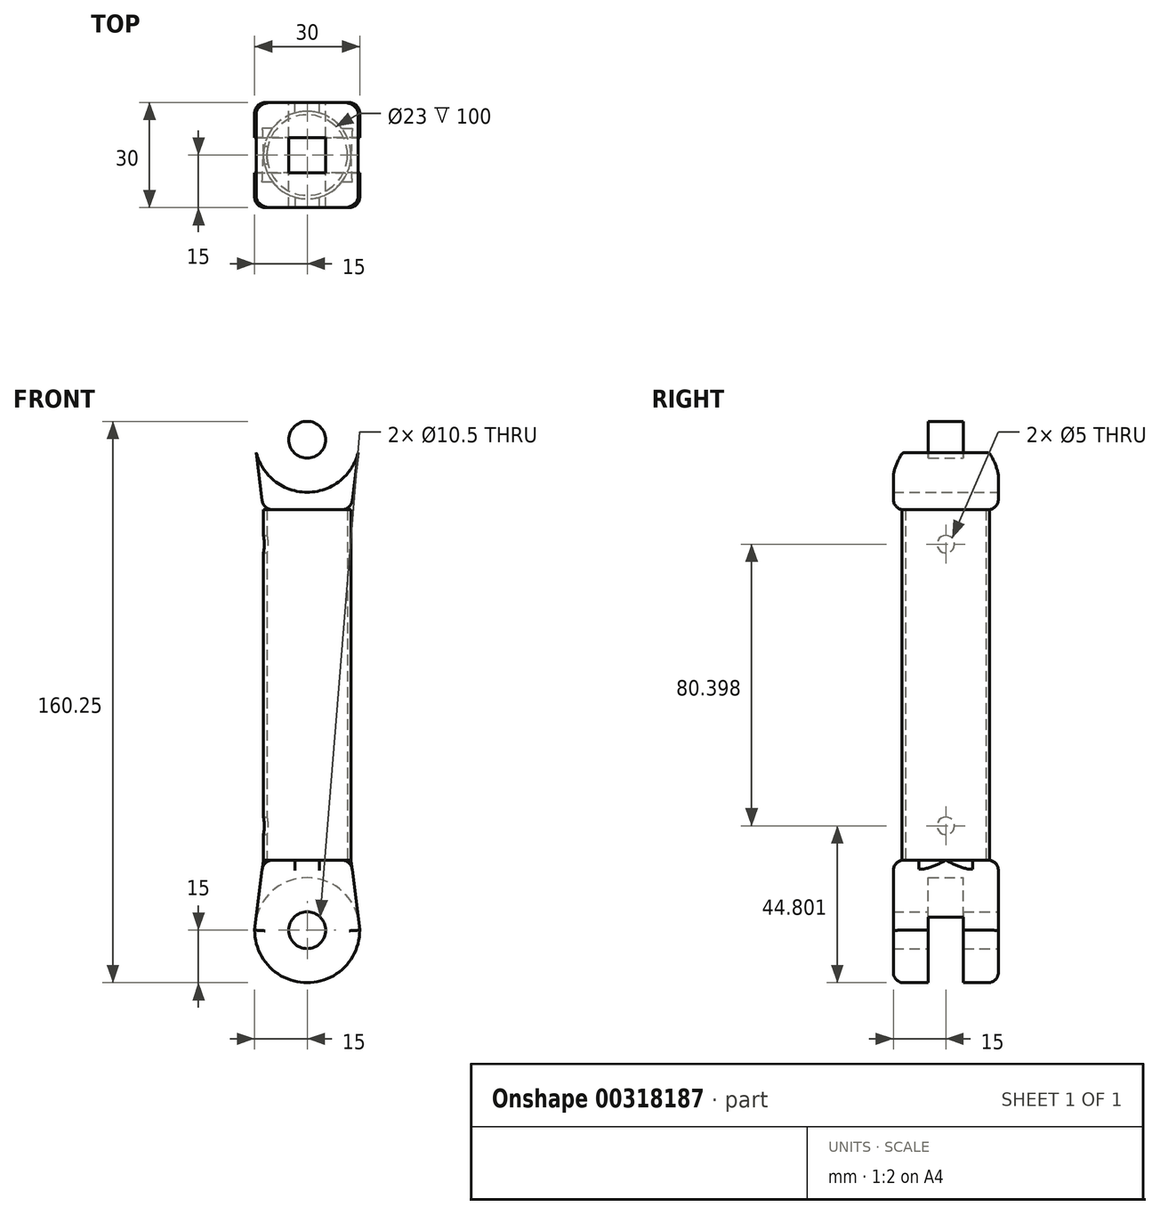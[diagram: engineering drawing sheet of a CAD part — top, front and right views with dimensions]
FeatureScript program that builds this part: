
annotation { "Feature Type Name" : "Feature", "Feature Type Description" : "" }
export const myFeature = defineFeature(function(context is Context, id is Id, definition is map)
    precondition{}
    {
        {
            var Q0;
            Q0=qCreatedBy(makeId("Front.planeOp"),FACE);
            var sketch = newSketch(context, id + "F0", { "sketchPlane" : qUnion([Q0])});
            skCircle(sketch, "E0", {"center": v(0, -70) * mm, "radius": 5.25 * mm});
            skCircle(sketch, "E1", {"center": v(0, -70) * mm, "radius": 15 * mm});
            skLineSegment(sketch, "E2", {"start": v(-12.5, -50) * mm, "end": v(12.5, -50) * mm});
            skLineSegment(sketch, "E3", {"start": v(-15, -69.99) * mm, "end": v(-12.5, -50) * mm});
            skLineSegment(sketch, "E4", {"start": v(15, -69.99) * mm, "end": v(12.5, -50) * mm});
            skCircle(sketch, "E5.MirrorC", {"center": v(0, 70) * mm, "radius": 15 * mm});
            skLineSegment(sketch, "E6.MirrorCS", {"start": v(15, 69.99) * mm, "end": v(12.5, 50) * mm});
            skLineSegment(sketch, "E7.MirrorCS", {"start": v(-12.5, 50) * mm, "end": v(12.5, 50) * mm});
            skLineSegment(sketch, "E8.MirrorCS", {"start": v(-15, 69.99) * mm, "end": v(-12.5, 50) * mm});
            skCircle(sketch, "E9.MirrorC", {"center": v(0, 70) * mm, "radius": 5.25 * mm});
            skSolve(sketch);
        }
        {
            var Q0;
            {var subQ5=sQuery(id+"F0.wireOp",EDGE,"E2");Q0=makeQuery(id+"F0.imprint","IMPRINT",FACE,{"disambiguationData":[TD([[makeQuery(id+"F0.imprint","IMPRINT",EDGE,{"derivedFrom":subQ5}),-1.0]])]});}
            var Q1;
            Q1=makeQuery(id+"F0.imprint","IMPRINT",FACE,{"disambiguationData":[TD([[makeQuery(id+"F0.imprint","IMPRINT",EDGE,{"derivedFrom":sQuery(id+"F0.wireOp",EDGE,"E0")}),-1.0]])]});
            extrude(context, id + "F1", {"entities" : qUnion([Q0, Q1]), "endBound" : BoundingType.SYMMETRIC, "depth" : 30 * mm});
        }
        {
            var Q0;
            Q0=qCreatedBy(makeId("Right.planeOp"),FACE);
            var sketch = newSketch(context, id + "F2", { "sketchPlane" : qUnion([Q0])});
            skLineSegment(sketch, "E10", {"start": v(0, -85) * mm, "end": v(5, -85) * mm});
            skLineSegment(sketch, "E11", {"start": v(5, -85) * mm, "end": v(5, -55) * mm});
            skLineSegment(sketch, "E12", {"start": v(5, -55) * mm, "end": v(-5, -55) * mm});
            skLineSegment(sketch, "E13", {"start": v(-5, -55) * mm, "end": v(-5, -85) * mm});
            skLineSegment(sketch, "E14", {"start": v(-5, -85) * mm, "end": v(0, -85) * mm});
            skSolve(sketch);
        }
        {
            var Q0;
            Q0 = qSketchRegion(id + "F2", true);
            extrude(context, id + "F3", {"entities" : qUnion([Q0]), "operationType" : NewBodyOperationType.REMOVE, "endBound" : BoundingType.SYMMETRIC, "oppositeDirection" : true, "depth" : 100 * mm});
        }
        {
            var Q0;
            {var subQ5=sQuery(id+"F0.wireOp",EDGE,"E2");Q0=makeQuery(id+"F0.imprint","IMPRINT",FACE,{"disambiguationData":[TD([[makeQuery(id+"F0.imprint","IMPRINT",EDGE,{"derivedFrom":subQ5}),-1.0]])]});}
            extrude(context, id + "F4", {"entities" : qUnion([Q0]), "operationType" : NewBodyOperationType.ADD, "endBound" : BoundingType.SYMMETRIC, "depth" : 25 * mm});
        }
        {
            var Q0;
            Q0=makeQuery(id+"F0.imprint","IMPRINT",FACE,{"disambiguationData":[TD([[makeQuery(id+"F0.imprint","IMPRINT",EDGE,{"derivedFrom":sQuery(id+"F0.wireOp",EDGE,"E9.MirrorC")}),1.0]])]});
            extrude(context, id + "F5", {"entities" : qUnion([Q0]), "endBound" : BoundingType.SYMMETRIC, "depth" : 10 * mm});
        }
        {
            var Q0;
            {var subQ5=sQuery(id+"F0.wireOp",EDGE,"E7.MirrorCS");Q0=makeQuery(id+"F0.imprint","IMPRINT",FACE,{"disambiguationData":[TD([[makeQuery(id+"F0.imprint","IMPRINT",EDGE,{"derivedFrom":subQ5}),1.0]])]});}
            extrude(context, id + "F6", {"entities" : qUnion([Q0]), "operationType" : NewBodyOperationType.ADD, "endBound" : BoundingType.SYMMETRIC, "depth" : 30 * mm});
        }
        {
            var Q0;
            Q0=qCreatedBy(makeId("Top.planeOp"),FACE);
            var sketch = newSketch(context, id + "F7", { "sketchPlane" : qUnion([Q0])});
            skCircle(sketch, "E15", {"center": v(0, 0) * mm, "radius": 12.5 * mm});
            skCircle(sketch, "E16", {"center": v(0, 0) * mm, "radius": 11.5 * mm});
            skSolve(sketch);
        }
        {
            var Q0;
            Q0 = qSketchRegion(id + "F7", true);
            extrude(context, id + "F8", {"entities" : qUnion([Q0]), "endBound" : BoundingType.SYMMETRIC, "depth" : 100 * mm});
        }
        {
            var Q0;
            Q0=makeQuery(id+"F1.opExtrude","SWEPT_BODY",BODY,{"disambiguationData":[OSD([sQuery(id+"F0.wireOp",EDGE,"E0"),sQuery(id+"F0.wireOp",EDGE,"E1"),sQuery(id+"F0.wireOp",EDGE,"E2"),sQuery(id+"F0.wireOp",EDGE,"E3"),sQuery(id+"F0.wireOp",EDGE,"E4")])]});
            var Q1;
            Q1=makeQuery(id+"F5.opExtrude","SWEPT_BODY",BODY,{"disambiguationData":[OSD([sQuery(id+"F0.wireOp",EDGE,"E5.MirrorC"),sQuery(id+"F0.wireOp",EDGE,"E6.MirrorCS"),sQuery(id+"F0.wireOp",EDGE,"E8.MirrorCS"),sQuery(id+"F0.wireOp",EDGE,"E9.MirrorC")])]});
            var Q2;
            Q2=makeQuery(id+"F8.opExtrude","SWEPT_BODY",BODY,{"disambiguationData":[OSD([sQuery(id+"F7.wireOp",EDGE,"E15"),sQuery(id+"F7.wireOp",EDGE,"E16")])]});
            booleanBodies(context, id + "F9", {"operationType" : BooleanOperationType.UNION, "tools" : qUnion([Q0, Q1, Q2])});
        }
        {
            var Q0;
            {var subQ0=sQuery(id+"F0.wireOp",EDGE,"E4");var subQ1=sQuery(id+"F0.wireOp",EDGE,"E2");Q0=makeQuery(id+"F9.opBoolean","SPLIT",EDGE,{"disambiguationData":[TD([makeQuery(id+"F1.opExtrude","CAP_FACE",FACE,{"disambiguationData":[OSD([sQuery(id+"F0.wireOp",EDGE,"E0"),sQuery(id+"F0.wireOp",EDGE,"E1"),subQ1,sQuery(id+"F0.wireOp",EDGE,"E3"),subQ0])],"isStart":true})])],"derivedFrom":makeQuery(id+"F1.opExtrude","SWEPT_EDGE",EDGE,{"disambiguationData":[OSD([subQ1,subQ0])]})});}
            var Q1;
            Q1=makeQuery(id+"F1.opExtrude","CAP_EDGE",EDGE,{"disambiguationData":[OSD([sQuery(id+"F0.wireOp",EDGE,"E4")])],"isStart":true});
            var Q2;
            Q2=makeQuery(id+"F1.opExtrude","CAP_EDGE",EDGE,{"disambiguationData":[OSD([sQuery(id+"F0.wireOp",EDGE,"E1")])],"isStart":true});
            var Q3;
            Q3=makeQuery(id+"F1.opExtrude","CAP_EDGE",EDGE,{"disambiguationData":[OSD([sQuery(id+"F0.wireOp",EDGE,"E3")])],"isStart":true});
            var Q4;
            Q4=makeQuery(id+"F1.opExtrude","CAP_EDGE",EDGE,{"disambiguationData":[OSD([sQuery(id+"F0.wireOp",EDGE,"E2")])],"isStart":true});
            var Q5;
            {var subQ0=sQuery(id+"F0.wireOp",EDGE,"E3");var subQ1=sQuery(id+"F0.wireOp",EDGE,"E2");Q5=makeQuery(id+"F9.opBoolean","SPLIT",EDGE,{"disambiguationData":[TD([makeQuery(id+"F1.opExtrude","CAP_FACE",FACE,{"disambiguationData":[OSD([sQuery(id+"F0.wireOp",EDGE,"E0"),sQuery(id+"F0.wireOp",EDGE,"E1"),subQ1,subQ0,sQuery(id+"F0.wireOp",EDGE,"E4")])],"isStart":true})])],"derivedFrom":makeQuery(id+"F1.opExtrude","SWEPT_EDGE",EDGE,{"disambiguationData":[OSD([subQ1,subQ0])]})});}
            var Q6;
            Q6=makeQuery(id+"F1.opExtrude","CAP_EDGE",EDGE,{"disambiguationData":[OSD([sQuery(id+"F0.wireOp",EDGE,"E3")])],"isStart":false});
            var Q7;
            Q7=makeQuery(id+"F1.opExtrude","CAP_EDGE",EDGE,{"disambiguationData":[OSD([sQuery(id+"F0.wireOp",EDGE,"E1")])],"isStart":false});
            var Q8;
            Q8=makeQuery(id+"F1.opExtrude","CAP_EDGE",EDGE,{"disambiguationData":[OSD([sQuery(id+"F0.wireOp",EDGE,"E4")])],"isStart":false});
            var Q9;
            Q9=makeQuery(id+"F1.opExtrude","CAP_EDGE",EDGE,{"disambiguationData":[OSD([sQuery(id+"F0.wireOp",EDGE,"E2")])],"isStart":false});
            var Q10;
            Q10=makeQuery(id+"F6.opExtrude","CAP_EDGE",EDGE,{"disambiguationData":[OSD([sQuery(id+"F0.wireOp",EDGE,"E7.MirrorCS")])],"isStart":true});
            var Q11;
            {var subQ0=sQuery(id+"F0.wireOp",EDGE,"E7.MirrorCS");var subQ1=sQuery(id+"F0.wireOp",EDGE,"E6.MirrorCS");Q11=makeQuery(id+"F9.opBoolean","SPLIT",EDGE,{"disambiguationData":[TD([makeQuery(id+"F6.opExtrude","CAP_FACE",FACE,{"disambiguationData":[OSD([sQuery(id+"F0.wireOp",EDGE,"E5.MirrorC"),subQ1,subQ0,sQuery(id+"F0.wireOp",EDGE,"E8.MirrorCS")])],"isStart":false})])],"derivedFrom":makeQuery(id+"F6.opExtrude","SWEPT_EDGE",EDGE,{"disambiguationData":[OSD([subQ1,subQ0])]})});}
            var Q12;
            {var subQ0=sQuery(id+"F0.wireOp",EDGE,"E8.MirrorCS");var subQ1=sQuery(id+"F0.wireOp",EDGE,"E7.MirrorCS");Q12=makeQuery(id+"F9.opBoolean","SPLIT",EDGE,{"disambiguationData":[TD([makeQuery(id+"F6.opExtrude","CAP_FACE",FACE,{"disambiguationData":[OSD([sQuery(id+"F0.wireOp",EDGE,"E5.MirrorC"),sQuery(id+"F0.wireOp",EDGE,"E6.MirrorCS"),subQ1,subQ0])],"isStart":true})])],"derivedFrom":makeQuery(id+"F6.opExtrude","SWEPT_EDGE",EDGE,{"disambiguationData":[OSD([subQ1,subQ0])]})});}
            var Q13;
            Q13=makeQuery(id+"F6.opExtrude","CAP_EDGE",EDGE,{"disambiguationData":[OSD([sQuery(id+"F0.wireOp",EDGE,"E7.MirrorCS")])],"isStart":false});
            var Q14;
            Q14=makeQuery(id+"F6.opExtrude","CAP_EDGE",EDGE,{"disambiguationData":[OSD([sQuery(id+"F0.wireOp",EDGE,"E6.MirrorCS")])],"isStart":false});
            var Q15;
            Q15=makeQuery(id+"F6.opExtrude","CAP_EDGE",EDGE,{"disambiguationData":[OSD([sQuery(id+"F0.wireOp",EDGE,"E8.MirrorCS")])],"isStart":false});
            var Q16;
            Q16=makeQuery(id+"F6.opExtrude","CAP_EDGE",EDGE,{"disambiguationData":[OSD([sQuery(id+"F0.wireOp",EDGE,"E6.MirrorCS")])],"isStart":true});
            var Q17;
            Q17=makeQuery(id+"F6.opExtrude","CAP_EDGE",EDGE,{"disambiguationData":[OSD([sQuery(id+"F0.wireOp",EDGE,"E8.MirrorCS")])],"isStart":true});
            fillet(context, id + "F10", {"entities" : qUnion([Q0, Q1, Q2, Q3, Q4, Q5, Q6, Q7, Q8, Q9, Q10, Q11, Q12, Q13, Q14, Q15, Q16, Q17]), "radius" : 3 * mm, "tangentPropagation" : true, "allowEdgeOverflow" : false});
        }
        {
            var Q0;
            Q0=qCreatedBy(makeId("Right.planeOp"),FACE);
            var sketch = newSketch(context, id + "F11", { "sketchPlane" : qUnion([Q0])});
            skCircle(sketch, "E17", {"center": v(0, -40.2) * mm, "radius": 2.5 * mm});
            skCircle(sketch, "E18.MirrorC", {"center": v(0, 40.2) * mm, "radius": 2.5 * mm});
            skSolve(sketch);
        }
        {
            var Q0;
            Q0 = qSketchRegion(id + "F11", true);
            extrude(context, id + "F12", {"entities" : qUnion([Q0]), "operationType" : NewBodyOperationType.REMOVE, "oppositeDirection" : true, "depth" : 100 * mm});
        }
    });
